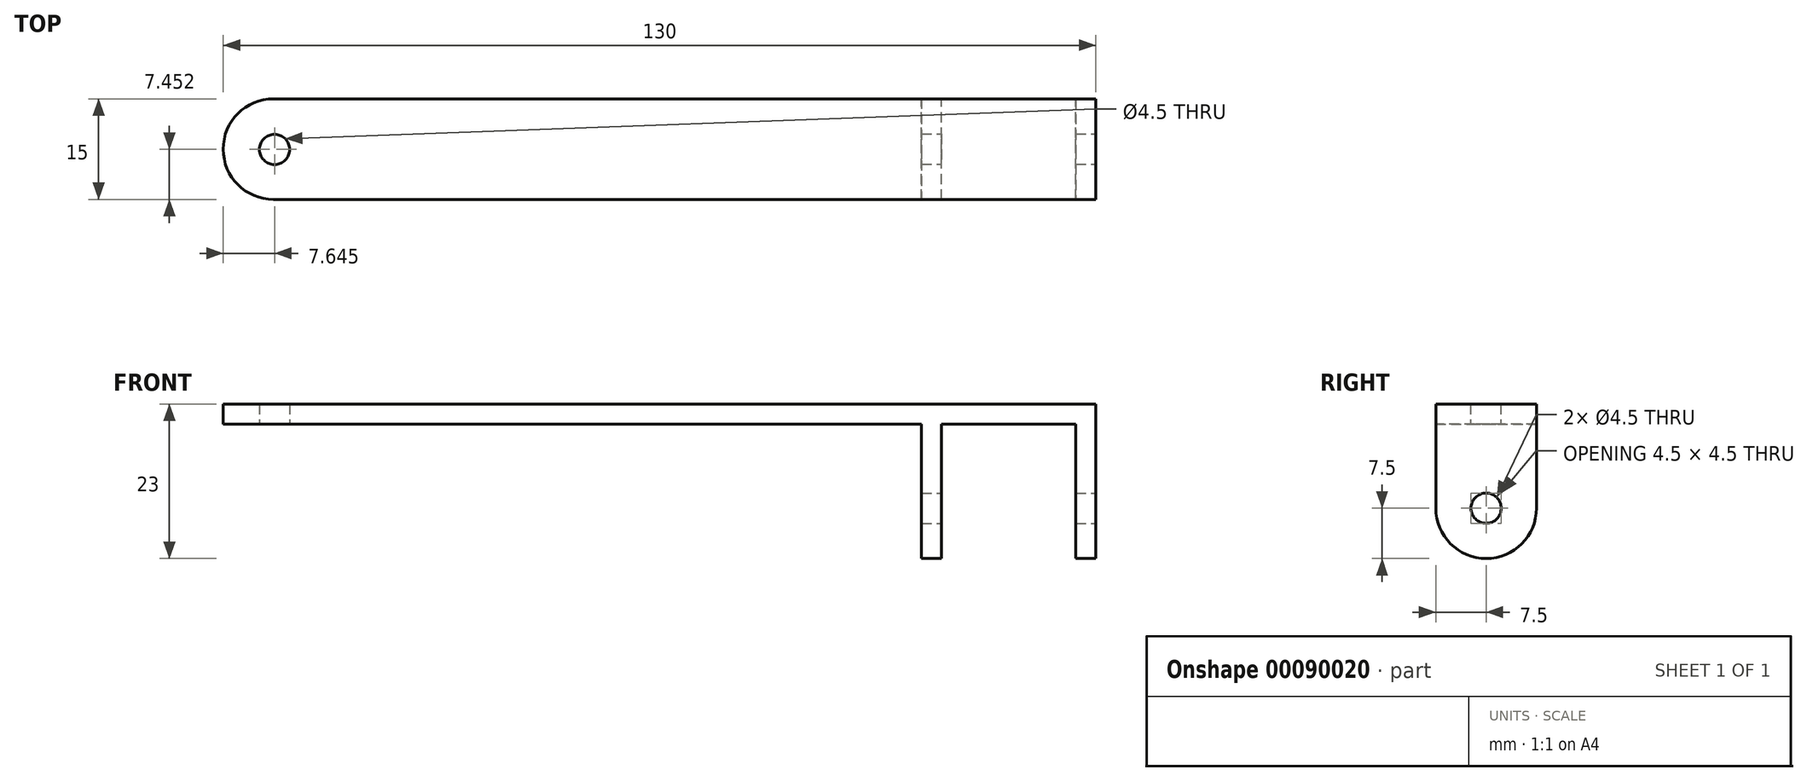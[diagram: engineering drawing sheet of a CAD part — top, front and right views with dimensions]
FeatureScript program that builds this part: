
annotation { "Feature Type Name" : "Feature", "Feature Type Description" : "" }
export const myFeature = defineFeature(function(context is Context, id is Id, definition is map)
    precondition{}
    {
        {
            var Q0;
            Q0=qCreatedBy(makeId("Front.planeOp"),FACE);
            var sketch = newSketch(context, id + "F0", { "sketchPlane" : qUnion([Q0])});
            skLineSegment(sketch, "E0.bottom", {"start": v(-80.18, 3) * mm, "end": v(49.82, 3) * mm});
            skLineSegment(sketch, "E0.top", {"start": v(-80.18, 0) * mm, "end": v(49.82, 0) * mm});
            skLineSegment(sketch, "E0.left", {"start": v(-80.18, 3) * mm, "end": v(-80.18, 0) * mm});
            skLineSegment(sketch, "E0.right", {"start": v(49.82, 3) * mm, "end": v(49.82, -20) * mm});
            skLineSegment(sketch, "E1", {"start": v(49.82, -20) * mm, "end": v(46.82, -20) * mm});
            skLineSegment(sketch, "E2", {"start": v(46.82, -20) * mm, "end": v(46.82, 0) * mm});
            skLineSegment(sketch, "E3", {"start": v(46.82, 0) * mm, "end": v(26.82, 0) * mm});
            skLineSegment(sketch, "E4", {"start": v(26.82, 0) * mm, "end": v(26.82, -20) * mm});
            skLineSegment(sketch, "E5", {"start": v(26.82, -20) * mm, "end": v(23.82, -20) * mm});
            skLineSegment(sketch, "E6", {"start": v(23.82, -20) * mm, "end": v(23.82, 0) * mm});
            skSolve(sketch);
        }
        {
            var Q0;
            {var subQ0=sQuery(id+"F0.wireOp",EDGE,"E4");Q0=makeQuery(id+"F0.imprint","IMPRINT",FACE,{"disambiguationData":[TD([[makeQuery(id+"F0.imprint","IMPRINT",EDGE,{"derivedFrom":subQ0}),-1.0]])]});}
            var Q1;
            {var subQ4=sQuery(id+"F0.wireOp",EDGE,"E1");Q1=makeQuery(id+"F0.imprint","IMPRINT",FACE,{"disambiguationData":[TD([[makeQuery(id+"F0.imprint","IMPRINT",EDGE,{"derivedFrom":subQ4}),-1.0]])]});}
            var Q2;
            {var subQ6=sQuery(id+"F0.wireOp",EDGE,"E0.bottom");Q2=makeQuery(id+"F0.imprint","IMPRINT",FACE,{"disambiguationData":[TD([[makeQuery(id+"F0.imprint","IMPRINT",EDGE,{"derivedFrom":subQ6}),-1.0]])]});}
            var Q3;
            Q3=sQuery(id+"F0.wireOp",EDGE,"E2");
            var Q4;
            Q4=sQuery(id+"F0.wireOp",EDGE,"E3");
            var Q5;
            Q5=sQuery(id+"F0.wireOp",EDGE,"E4");
            var Q6;
            Q6=sQuery(id+"F0.wireOp",EDGE,"E6");
            var Q7;
            Q7=sQuery(id+"F0.wireOp",EDGE,"E0.right");
            var Q8;
            Q8=sQuery(id+"F0.wireOp",EDGE,"E0.top");
            var Q9;
            Q9=sQuery(id+"F0.wireOp",EDGE,"E0.bottom");
            var Q10;
            Q10=sQuery(id+"F0.wireOp",EDGE,"E5");
            var Q11;
            Q11=sQuery(id+"F0.wireOp",EDGE,"E1");
            var Q12;
            Q12=sQuery(id+"F0.wireOp",EDGE,"E0.left");
            extrude(context, id + "F1", {"entities" : qUnion([Q0, Q1, Q2]), "surfaceEntities" : qUnion([Q3, Q4, Q5, Q6, Q7, Q8, Q9, Q10, Q11, Q12]), "depth" : 15 * mm});
        }
        {
            var Q0;
            Q0=qCreatedBy(makeId("Top.planeOp"),FACE);
            var sketch = newSketch(context, id + "F2", { "sketchPlane" : qUnion([Q0])});
            skPoint(sketch, "E7", {"position": v(-80.03, -7.55) * mm});
            skPoint(sketch, "E8", {"position": v(-72.53, -7.55) * mm});
            skSolve(sketch);
        }
        {
            var Q0;
            Q0=sQuery(id+"F2.wireOp",VERTEX,"E8");
            var Q1;
            Q1=makeQuery(id+"F1.opExtrude","SWEPT_BODY",BODY,{"disambiguationData":[OSD([sQuery(id+"F0.wireOp",EDGE,"E0.bottom"),sQuery(id+"F0.wireOp",EDGE,"E0.top"),sQuery(id+"F0.wireOp",EDGE,"E0.left"),sQuery(id+"F0.wireOp",EDGE,"E0.right"),sQuery(id+"F0.wireOp",EDGE,"E1"),sQuery(id+"F0.wireOp",EDGE,"E2"),sQuery(id+"F0.wireOp",EDGE,"E3"),sQuery(id+"F0.wireOp",EDGE,"E4"),sQuery(id+"F0.wireOp",EDGE,"E5"),sQuery(id+"F0.wireOp",EDGE,"E6")])]});
            hole(context, id + "F3", {"style" : HoleStyle.SIMPLE, "endStyle" : HoleEndStyle.BLIND, "oppositeDirection" : true, "holeDiameter" : 4.5 * mm, "holeDepth" : 4 * mm, "locations" : qUnion([Q0]), "scope" : qUnion([Q1])});
        }
        {
            var Q0;
            Q0=makeQuery(id+"F1.opExtrude","SWEPT_FACE",FACE,{"disambiguationData":[OSD([sQuery(id+"F0.wireOp",EDGE,"E0.right")])]});
            var sketch = newSketch(context, id + "F4", { "sketchPlane" : qUnion([Q0])});
            skPoint(sketch, "E9", {"position": v(-7.5, -20) * mm});
            skPoint(sketch, "E10", {"position": v(-7.5, -12.5) * mm});
            skSolve(sketch);
        }
        {
            var Q0;
            Q0=sQuery(id+"F4.wireOp",VERTEX,"E10");
            var Q1;
            Q1=makeQuery(id+"F1.opExtrude","SWEPT_BODY",BODY,{"disambiguationData":[OSD([sQuery(id+"F0.wireOp",EDGE,"E0.bottom"),sQuery(id+"F0.wireOp",EDGE,"E0.top"),sQuery(id+"F0.wireOp",EDGE,"E0.left"),sQuery(id+"F0.wireOp",EDGE,"E0.right"),sQuery(id+"F0.wireOp",EDGE,"E1"),sQuery(id+"F0.wireOp",EDGE,"E2"),sQuery(id+"F0.wireOp",EDGE,"E3"),sQuery(id+"F0.wireOp",EDGE,"E4"),sQuery(id+"F0.wireOp",EDGE,"E5"),sQuery(id+"F0.wireOp",EDGE,"E6")])]});
            hole(context, id + "F5", {"style" : HoleStyle.SIMPLE, "endStyle" : HoleEndStyle.THROUGH, "holeDiameter" : 4.5 * mm, "locations" : qUnion([Q0]), "scope" : qUnion([Q1]), "isTappedThrough" : true});
        }
        {
            var Q0;
            Q0=makeQuery(id+"F1.opExtrude","CAP_EDGE",EDGE,{"disambiguationData":[OSD([sQuery(id+"F0.wireOp",EDGE,"E1")])],"isStart":true});
            fillet(context, id + "F6", {"entities" : qUnion([Q0]), "radius" : 7.5 * mm, "tangentPropagation" : true, "allowEdgeOverflow" : false});
        }
        {
            var Q0;
            Q0=makeQuery(id+"F1.opExtrude","CAP_EDGE",EDGE,{"disambiguationData":[OSD([sQuery(id+"F0.wireOp",EDGE,"E5")])],"isStart":false});
            var Q1;
            Q1=makeQuery(id+"F1.opExtrude","CAP_EDGE",EDGE,{"disambiguationData":[OSD([sQuery(id+"F0.wireOp",EDGE,"E1")])],"isStart":false});
            var Q2;
            Q2=makeQuery(id+"F1.opExtrude","CAP_EDGE",EDGE,{"disambiguationData":[OSD([sQuery(id+"F0.wireOp",EDGE,"E5")])],"isStart":true});
            var Q3;
            Q3=makeQuery(id+"F1.opExtrude","CAP_EDGE",EDGE,{"disambiguationData":[OSD([sQuery(id+"F0.wireOp",EDGE,"E0.left")])],"isStart":true});
            var Q4;
            Q4=makeQuery(id+"F1.opExtrude","CAP_EDGE",EDGE,{"disambiguationData":[OSD([sQuery(id+"F0.wireOp",EDGE,"E0.left")])],"isStart":false});
            fillet(context, id + "F7", {"entities" : qUnion([Q0, Q1, Q2, Q3, Q4]), "radius" : 7.5 * mm, "tangentPropagation" : true, "allowEdgeOverflow" : false});
        }
    });
